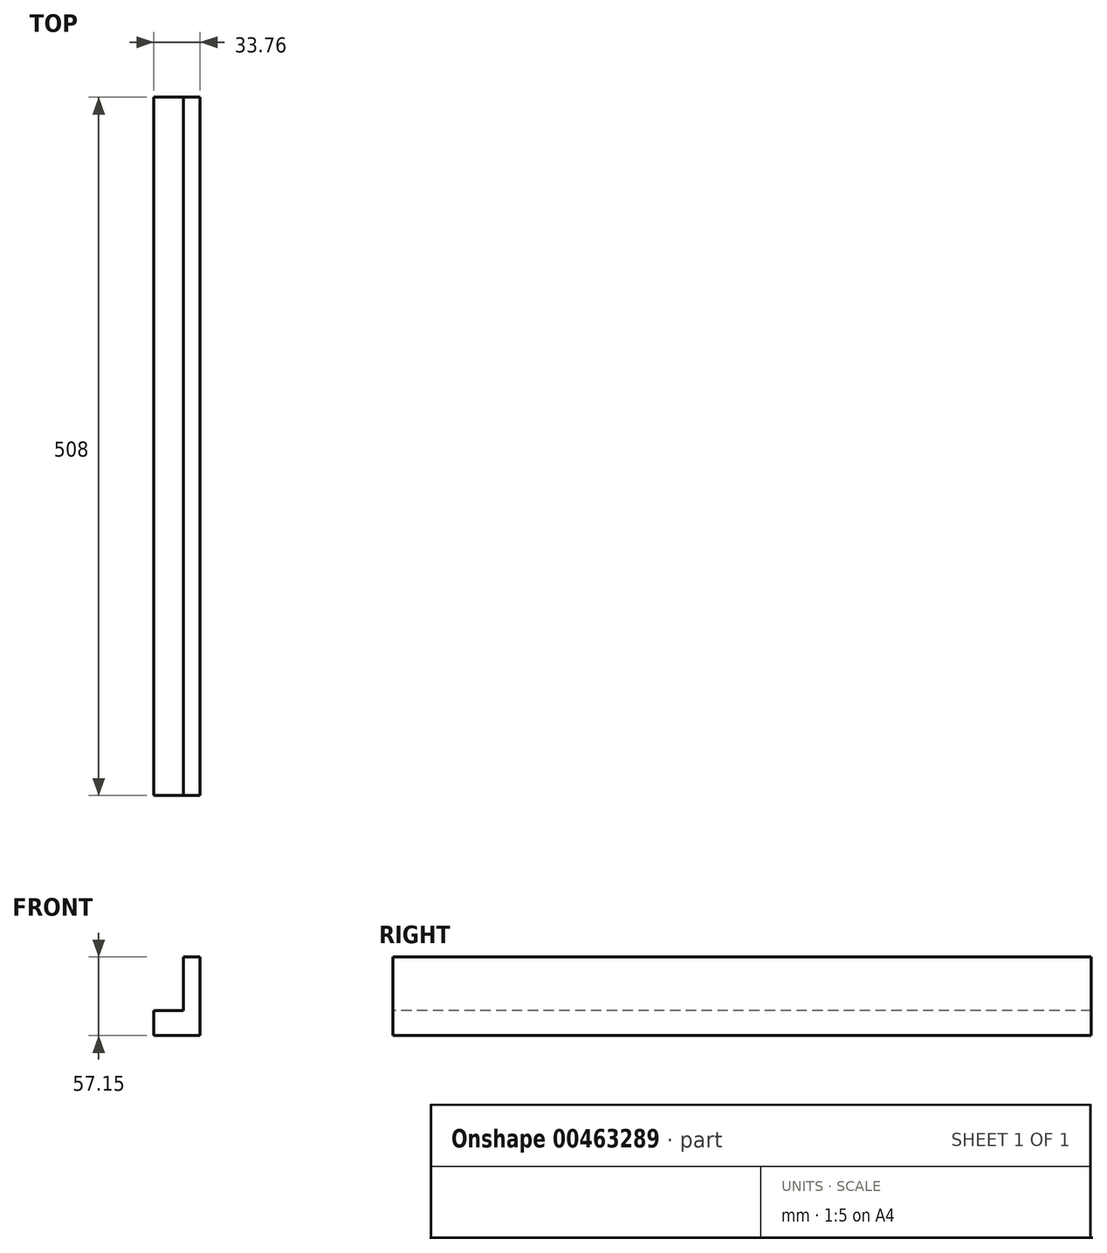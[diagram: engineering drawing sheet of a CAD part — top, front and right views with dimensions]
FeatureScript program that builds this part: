
annotation { "Feature Type Name" : "Feature", "Feature Type Description" : "" }
export const myFeature = defineFeature(function(context is Context, id is Id, definition is map)
    precondition{}
    {
        {
            var Q0;
            Q0=qCreatedBy(makeId("Front.planeOp"),FACE);
            var sketch = newSketch(context, id + "F0", { "sketchPlane" : qUnion([Q0])});
            skLineSegment(sketch, "E0", {"start": v(-58.74, 0) * mm, "end": v(-58.74, 38.8) * mm});
            skLineSegment(sketch, "E1", {"start": v(-58.74, 38.8) * mm, "end": v(-46.52, 38.8) * mm});
            skLineSegment(sketch, "E2", {"start": v(-46.52, 38.8) * mm, "end": v(-46.52, 0) * mm});
            skLineSegment(sketch, "E3", {"start": v(-46.52, 0) * mm, "end": v(-46.52, -18.34) * mm});
            skLineSegment(sketch, "E4", {"start": v(-46.52, -18.34) * mm, "end": v(-80.28, -18.34) * mm});
            skLineSegment(sketch, "E5", {"start": v(-80.28, -18.34) * mm, "end": v(-80.28, 0) * mm});
            skLineSegment(sketch, "E6", {"start": v(-80.28, 0) * mm, "end": v(-58.74, 0) * mm});
            skSolve(sketch);
        }
        {
            var Q0;
            Q0 = qSketchRegion(id + "F0", true);
            extrude(context, id + "F1", {"entities" : qUnion([Q0]), "oppositeDirection" : true, "depth" : 508 * mm});
        }
    });
